# Revit family: 3702A NX Fixture Dual Smart Port Adapter
name_source: partatom
category: Communication Devices
units: mm (PartAtom-declared; Revit-internal decimal feet)

## family parameters
Cut with Voids When Loaded = No
Host = Face
Maintain Annotation Orientation = No
OmniClass Number = 23.85.80.11.27
OmniClass Title = Lighting Controls
Part Type = Normal
Room Calculation Point = No
Round Connector Dimension = Use Diameter
Shared = Yes

## types (1)
- 3702A NX Fixture Dual Smart Port Adapter
    Assembly Code = D5090
    Black = Paint -  Carbon Black
    Default Elevation = 48 "
    Description = The Control Solutions NXFSP and NXDSP dual SmartPORT™ adapters allow for wired CAT5 interconnection of luminaires equipped with internal NXFM In-fixture modules.
    Features = Attractive, architecturally-pleasing decorator style design
• Gang-able with other decorator type devices
• Up to six buttons in a single gang
• Plug and play integration with NX SmartPORT
• Five-year limited warranty
• Low voltage device: 24 VDC
• Delivers simplified configuration and control of  Lighting
luminaires using SpectraSync™ color tuning technology
    Height = 18.26 "
    Manufacturer = NX Lighting Controls
    Model = NX Fixture Dual Smart Port Adapter
    Standby Power = 120VAC: 0.1,277VAC: 0.1,347VAC: 0.4
    Type Comments = NX Fixture Dual Smart Port Adapter
    URL = https://www.currentlighting.com
    Warranty = 5-Years Warranty
    White = Paint -  Matte White
    Width = 14.5 "

## geometry (parser evidence)
native form markers: Sweep x2
no freeform markers — native parametric forms only
